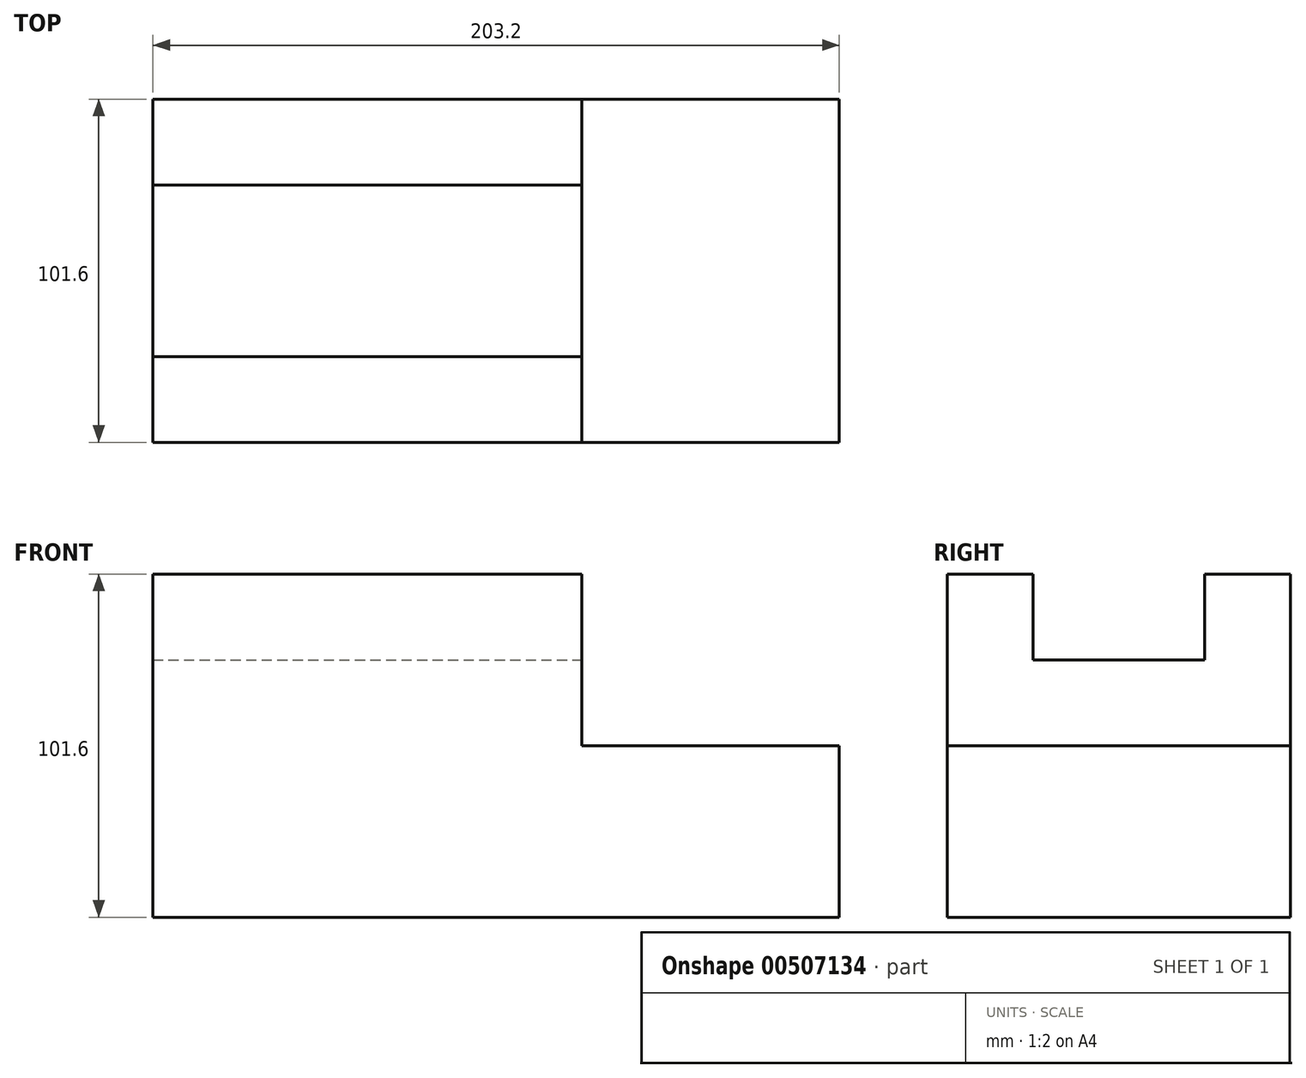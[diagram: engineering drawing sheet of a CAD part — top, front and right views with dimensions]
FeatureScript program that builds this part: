
annotation { "Feature Type Name" : "Feature", "Feature Type Description" : "" }
export const myFeature = defineFeature(function(context is Context, id is Id, definition is map)
    precondition{}
    {
        {
            var Q0;
            Q0=qCreatedBy(makeId("Front.planeOp"),FACE);
            var sketch = newSketch(context, id + "F0", { "sketchPlane" : qUnion([Q0])});
            skLineSegment(sketch, "E0.bottom", {"start": v(101.6, -50.8) * mm, "end": v(-101.6, -50.8) * mm});
            skLineSegment(sketch, "E0.top", {"start": v(101.6, 50.8) * mm, "end": v(-101.6, 50.8) * mm});
            skLineSegment(sketch, "E0.left", {"start": v(101.6, -50.8) * mm, "end": v(101.6, 50.8) * mm});
            skLineSegment(sketch, "E0.right", {"start": v(-101.6, -50.8) * mm, "end": v(-101.6, 50.8) * mm});
            skPoint(sketch, "E0.middle", {"position": v(0, 0) * mm});
            skLineSegment(sketch, "E1.bottom", {"start": v(101.6, 50.8) * mm, "end": v(25.4, 50.8) * mm});
            skLineSegment(sketch, "E1.top", {"start": v(101.6, 0) * mm, "end": v(25.4, 0) * mm});
            skLineSegment(sketch, "E1.left", {"start": v(101.6, 50.8) * mm, "end": v(101.6, 0) * mm});
            skLineSegment(sketch, "E1.right", {"start": v(25.4, 50.8) * mm, "end": v(25.4, 0) * mm});
            skSolve(sketch);
        }
        {
            var Q0;
            Q0=makeQuery(id+"F0.imprint","IMPRINT",FACE,{"disambiguationData":[TD([[makeQuery(id+"F0.imprint","IMPRINT",EDGE,{"derivedFrom":sQuery(id+"F0.wireOp",EDGE,"E0.bottom")}),-1.0]])]});
            extrude(context, id + "F1", {"entities" : qUnion([Q0]), "depth" : 101.6 * mm});
        }
        {
            var Q0;
            Q0=makeQuery(id+"F1.opExtrude","SWEPT_FACE",FACE,{"disambiguationData":[OSD([sQuery(id+"F0.wireOp",EDGE,"E0.top")])]});
            var sketch = newSketch(context, id + "F2", { "sketchPlane" : qUnion([Q0])});
            skLineSegment(sketch, "E2.bottom", {"start": v(-101.6, -25.4) * mm, "end": v(25.4, -25.4) * mm});
            skLineSegment(sketch, "E2.top", {"start": v(-101.6, -76.2) * mm, "end": v(25.4, -76.2) * mm});
            skLineSegment(sketch, "E2.left", {"start": v(-101.6, -25.4) * mm, "end": v(-101.6, -76.2) * mm});
            skLineSegment(sketch, "E2.right", {"start": v(25.4, -25.4) * mm, "end": v(25.4, -76.2) * mm});
            skSolve(sketch);
        }
        {
            var Q0;
            Q0=makeQuery(id+"F2.imprint","IMPRINT",FACE,{"disambiguationData":[TD([[makeQuery(id+"F2.imprint","IMPRINT",EDGE,{"derivedFrom":sQuery(id+"F2.wireOp",EDGE,"E2.bottom")}),-1.0]])]});
            extrude(context, id + "F3", {"entities" : qUnion([Q0]), "operationType" : NewBodyOperationType.REMOVE, "oppositeDirection" : true, "depth" : 25.4 * mm});
        }
    });
